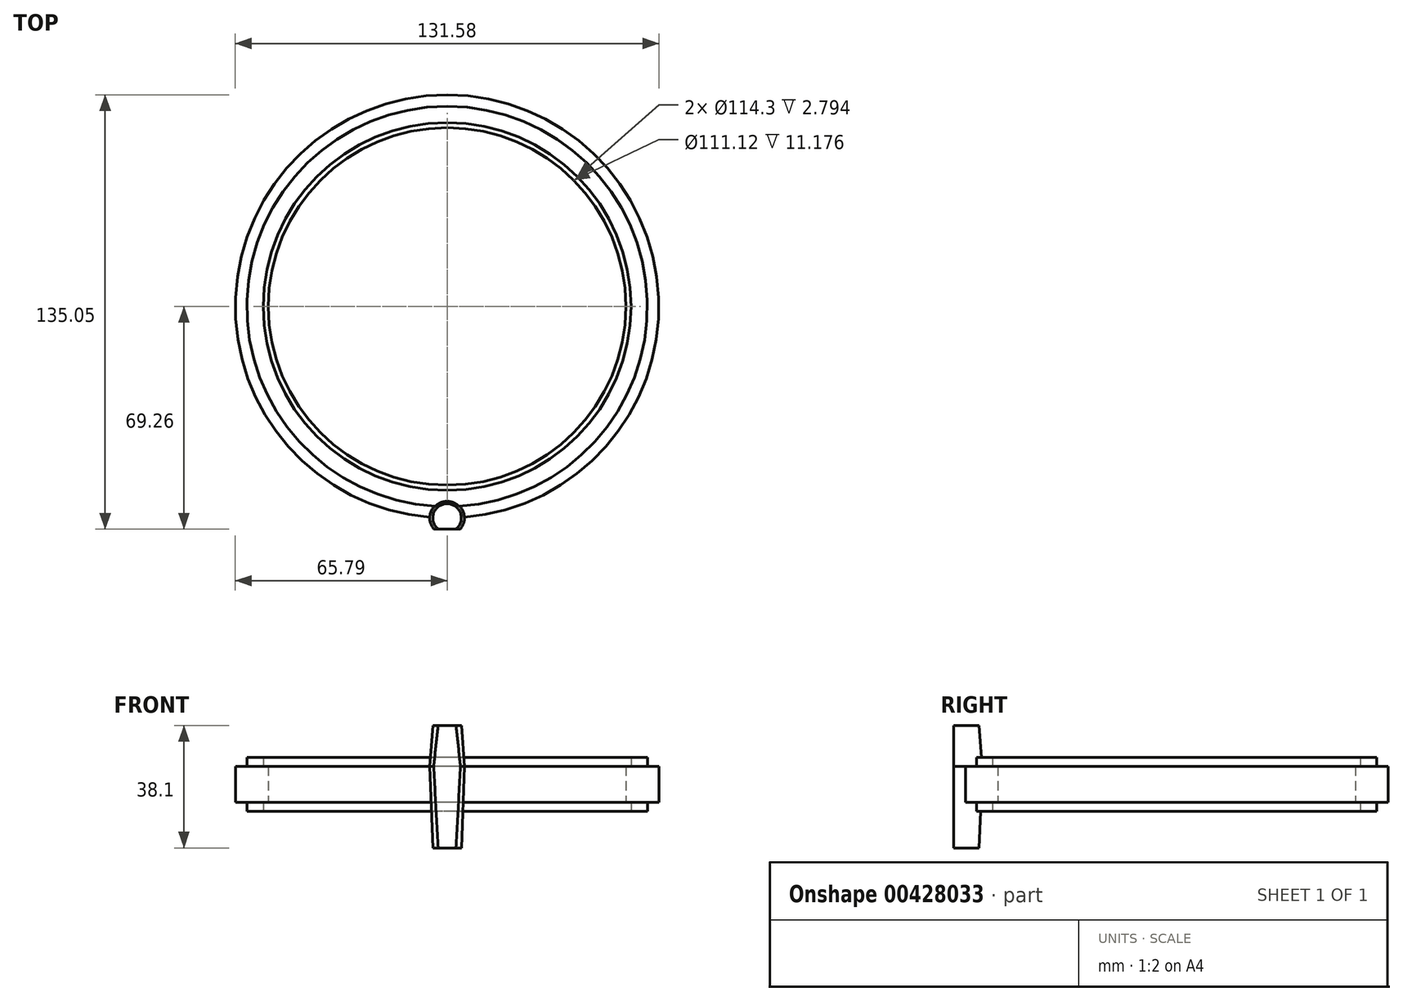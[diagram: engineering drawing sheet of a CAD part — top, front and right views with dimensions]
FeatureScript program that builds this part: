
annotation { "Feature Type Name" : "Feature", "Feature Type Description" : "" }
export const myFeature = defineFeature(function(context is Context, id is Id, definition is map)
    precondition{}
    {
        {
            var Q0;
            Q0=qCreatedBy(makeId("Top.planeOp"),FACE);
            var sketch = newSketch(context, id + "F0", { "sketchPlane" : qUnion([Q0])});
            skCircle(sketch, "E0", {"center": v(0, 0) * mm, "radius": 65.79 * mm});
            skCircle(sketch, "E1", {"center": v(0, 0) * mm, "radius": 55.56 * mm});
            skCircle(sketch, "E2", {"center": v(0, 0) * mm, "radius": 62.23 * mm});
            skCircle(sketch, "E3", {"center": v(0, 0) * mm, "radius": 57.15 * mm});
            skSolve(sketch);
        }
        {
            var Q0;
            Q0=makeQuery(id+"F0.imprint","IMPRINT",FACE,{"disambiguationData":[TD([[makeQuery(id+"F0.imprint","IMPRINT",EDGE,{"derivedFrom":sQuery(id+"F0.wireOp",EDGE,"E1")}),-1.0]])]});
            var Q1;
            Q1=makeQuery(id+"F0.imprint","IMPRINT",FACE,{"disambiguationData":[TD([[makeQuery(id+"F0.imprint","IMPRINT",EDGE,{"derivedFrom":sQuery(id+"F0.wireOp",EDGE,"E2")}),1.0]])]});
            var Q2;
            Q2=makeQuery(id+"F0.imprint","IMPRINT",FACE,{"disambiguationData":[TD([[makeQuery(id+"F0.imprint","IMPRINT",EDGE,{"derivedFrom":sQuery(id+"F0.wireOp",EDGE,"E0")}),1.0]])]});
            extrude(context, id + "F1", {"entities" : qUnion([Q0, Q1, Q2]), "endBound" : BoundingType.SYMMETRIC, "depth" : 11.18 * mm});
        }
        {
            var Q0;
            Q0=makeQuery(id+"F0.imprint","IMPRINT",FACE,{"disambiguationData":[TD([[makeQuery(id+"F0.imprint","IMPRINT",EDGE,{"derivedFrom":sQuery(id+"F0.wireOp",EDGE,"E2")}),1.0]])]});
            extrude(context, id + "F2", {"entities" : qUnion([Q0]), "operationType" : NewBodyOperationType.ADD, "endBound" : BoundingType.SYMMETRIC, "depth" : 16.76 * mm});
        }
        {
            var Q0;
            Q0=qCreatedBy(makeId("Top.planeOp"),FACE);
            cPlane(context, id + "F3", {"entities" : qUnion([Q0]), "cplaneType" : CPlaneType.OFFSET, "offset" : 5.6 * mm, "width" : 152.4 * mm, "height" : 152.4 * mm});
        }
        {
            var Q0;
            Q0=qCreatedBy(id+"F3.planeOp",FACE);
            var sketch = newSketch(context, id + "F4", { "sketchPlane" : qUnion([Q0])});
            skCircle(sketch, "E4", {"center": v(0, -65.79) * mm, "radius": 5.4 * mm});
            skSolve(sketch);
        }
        {
            var Q0;
            Q0=qCreatedBy(id+"F3.planeOp",FACE);
            cPlane(context, id + "F5", {"entities" : qUnion([Q0]), "cplaneType" : CPlaneType.OFFSET, "offset" : 12.7 * mm, "width" : 152.4 * mm, "height" : 152.4 * mm});
        }
        {
            var Q0;
            Q0=qCreatedBy(id+"F3.planeOp",FACE);
            cPlane(context, id + "F6", {"entities" : qUnion([Q0]), "cplaneType" : CPlaneType.OFFSET, "offset" : 25.4 * mm, "oppositeDirection" : true, "width" : 152.4 * mm, "height" : 152.4 * mm});
        }
        {
            var Q0;
            Q0=qCreatedBy(id+"F5.planeOp",FACE);
            var sketch = newSketch(context, id + "F7", { "sketchPlane" : qUnion([Q0])});
            skCircle(sketch, "E5", {"center": v(0, -65.79) * mm, "radius": 4.45 * mm});
            skSolve(sketch);
        }
        {
            var Q1;
            Q1=makeQuery(id+"F4.imprint","IMPRINT",FACE,{"disambiguationData":[TD([[makeQuery(id+"F4.imprint","IMPRINT",EDGE,{"derivedFrom":sQuery(id+"F4.wireOp",EDGE,"E4")}),1.0]])]});
            var Q2;
            Q2=makeQuery(id+"F7.imprint","IMPRINT",FACE,{"disambiguationData":[TD([[makeQuery(id+"F7.imprint","IMPRINT",EDGE,{"derivedFrom":sQuery(id+"F7.wireOp",EDGE,"E5")}),1.0]])]});
            loft(context, id + "F8", {"operationType" : NewBodyOperationType.ADD, "sheetProfilesArray" : [{ "sheetProfileEntities" : qUnion([Q1]) }, { "sheetProfileEntities" : qUnion([Q2]) }]});
        }
        {
            var Q0;
            Q0=qCreatedBy(id+"F6.planeOp",FACE);
            var sketch = newSketch(context, id + "F9", { "sketchPlane" : qUnion([Q0])});
            skCircle(sketch, "E6", {"center": v(0, -65.79) * mm, "radius": 4.45 * mm});
            skSolve(sketch);
        }
        {
            var Q1;
            Q1=makeQuery(id+"F4.imprint","IMPRINT",FACE,{"disambiguationData":[TD([[makeQuery(id+"F4.imprint","IMPRINT",EDGE,{"derivedFrom":sQuery(id+"F4.wireOp",EDGE,"E4")}),1.0]])]});
            var Q2;
            Q2=makeQuery(id+"F9.imprint","IMPRINT",FACE,{"disambiguationData":[TD([[makeQuery(id+"F9.imprint","IMPRINT",EDGE,{"derivedFrom":sQuery(id+"F9.wireOp",EDGE,"E6")}),1.0]])]});
            loft(context, id + "F10", {"operationType" : NewBodyOperationType.ADD, "sheetProfilesArray" : [{ "sheetProfileEntities" : qUnion([Q1]) }, { "sheetProfileEntities" : qUnion([Q2]) }]});
        }
        {
            var Q0;
            Q0=qCreatedBy(id+"F3.planeOp",FACE);
            var sketch = newSketch(context, id + "F11", { "sketchPlane" : qUnion([Q0])});
            skLineSegment(sketch, "E7", {"start": v(-4.13, -69.26) * mm, "end": v(4.13, -69.26) * mm});
            skArc(sketch, "E8", {"start": v(4.13, -69.26) * mm, "mid": v(0, -71.18) * mm, "end": v(-4.13, -69.26) * mm});
            skSolve(sketch);
        }
        {
            var Q0;
            Q0=makeQuery(id+"F11.imprint","IMPRINT",FACE,{"disambiguationData":[TD([[makeQuery(id+"F11.imprint","IMPRINT",EDGE,{"derivedFrom":sQuery(id+"F11.wireOp",EDGE,"E7")}),-1.0]])]});
            extrude(context, id + "F12", {"entities" : qUnion([Q0]), "operationType" : NewBodyOperationType.REMOVE, "endBound" : BoundingType.SYMMETRIC, "oppositeDirection" : true, "depth" : 76.2 * mm});
        }
    });
